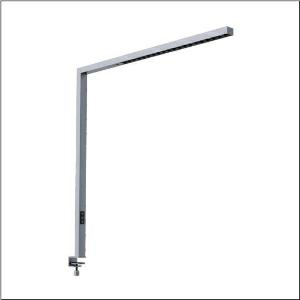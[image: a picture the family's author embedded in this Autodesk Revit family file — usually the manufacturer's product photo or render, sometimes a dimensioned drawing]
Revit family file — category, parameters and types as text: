
# Revit family: silica_r__31_desk_51my52ga4cs_0282
name_source: partatom
category: Lighting Fixtures
units: mm (PartAtom-declared; Revit-internal decimal feet)

## family parameters
Cut with Voids When Loaded = No
Host = Face
Light Source = No
Part Type = Normal
Room Calculation Point = No
Round Connector Dimension = Use Diameter
Shared = No

## types (1)
- Silica® 31 Desk (1 x LED, 10600 lm, 75 W, 4000K)
    Apparent Load = 75 VA
    CIE Flux Codes = 86 100 100 24 100
    Color Rendering = 80
    Color Temperature = 4000K
    Default Elevation = 1800 mm
    Description = Silica® 31 Desk, desktop luminaire, secondary optical cover: cover panel, of PMMA, light emission: direct/indirect distribution, primary light characteristic: symmetric, installation type: as desk luminaire, LED, rated luminous flux: 10.600lm, luminous efficacy: 141lm/W, light colour: 840, colour temperature: 4000K, daylight-dependent control, with cable with plug, mains connection: 230V, AC, 50Hz, connection cable pre-assembled, rated input power: 75W, luminaire head, of aluminium, metallic grey (RAL 9006), length: 1.203mm, width: 52mm, supporting column, angular, of aluminium, metallic grey (RAL 9006), baseplate, of steel, metallic grey (RAL 9006), protection rating (complete): IP20, insulation class (complete): insulation class I (protective earthing), certification: CE, permissible operating ambient temperature: -20..+40°C, standard: EN 50419, packaging unit: 1 piece
    Height = 36 mm
    Lamp = 1 x LED
    Lamp Light Flux = 10600 lm
    Lamp Power = 75 W
    Lamp count = 1
    Length = 1203 mm
    Luminous efficacy = 141 lm/W
    Manufacturer = Siteco
    ModVariant = No
    Model = 51MY52GA4CS
    Mounting Place = Floor
    Mounting Type = Freestanding
    Number of Poles = 1
    OnlyDefault = Yes
    Power Factor = 1
    Product Name = Silica® 31 Desk
    Product group = desktop luminaire
    ProductGroupID = 1302
    Protection Class = Protection class I
    Protection Degree = IP 20
    RLX_Detail_Level = 1
    RLX_Emergency_Light_Flux = 0 lm
    RLX_Emergency_Type = 0
    RLX_Emergency_Type_DB = No
    RlxData = <blob elided: 19617 chars, md5=8cca862d>
    Socket = socket
    Standby Power = 0 W
    System Light Flux = 10600 lm
    System Power = 75 W
    Type Comments = Product without accessories
    Type Image = l_1275333.jpg
    URL = http://relux.com
    VarID = ---
    Voltage = 0 V
    Weight = 0.00 kg
    Width = 52 mm  [stored 0.170604 ft]

note: [stored X ft] marks values corroborated as IEEE doubles in the binary element streams (Revit-internal decimal feet)

## geometry (parser evidence)
native form markers: Blend x4, Sweep x17
no freeform markers — native parametric forms only
